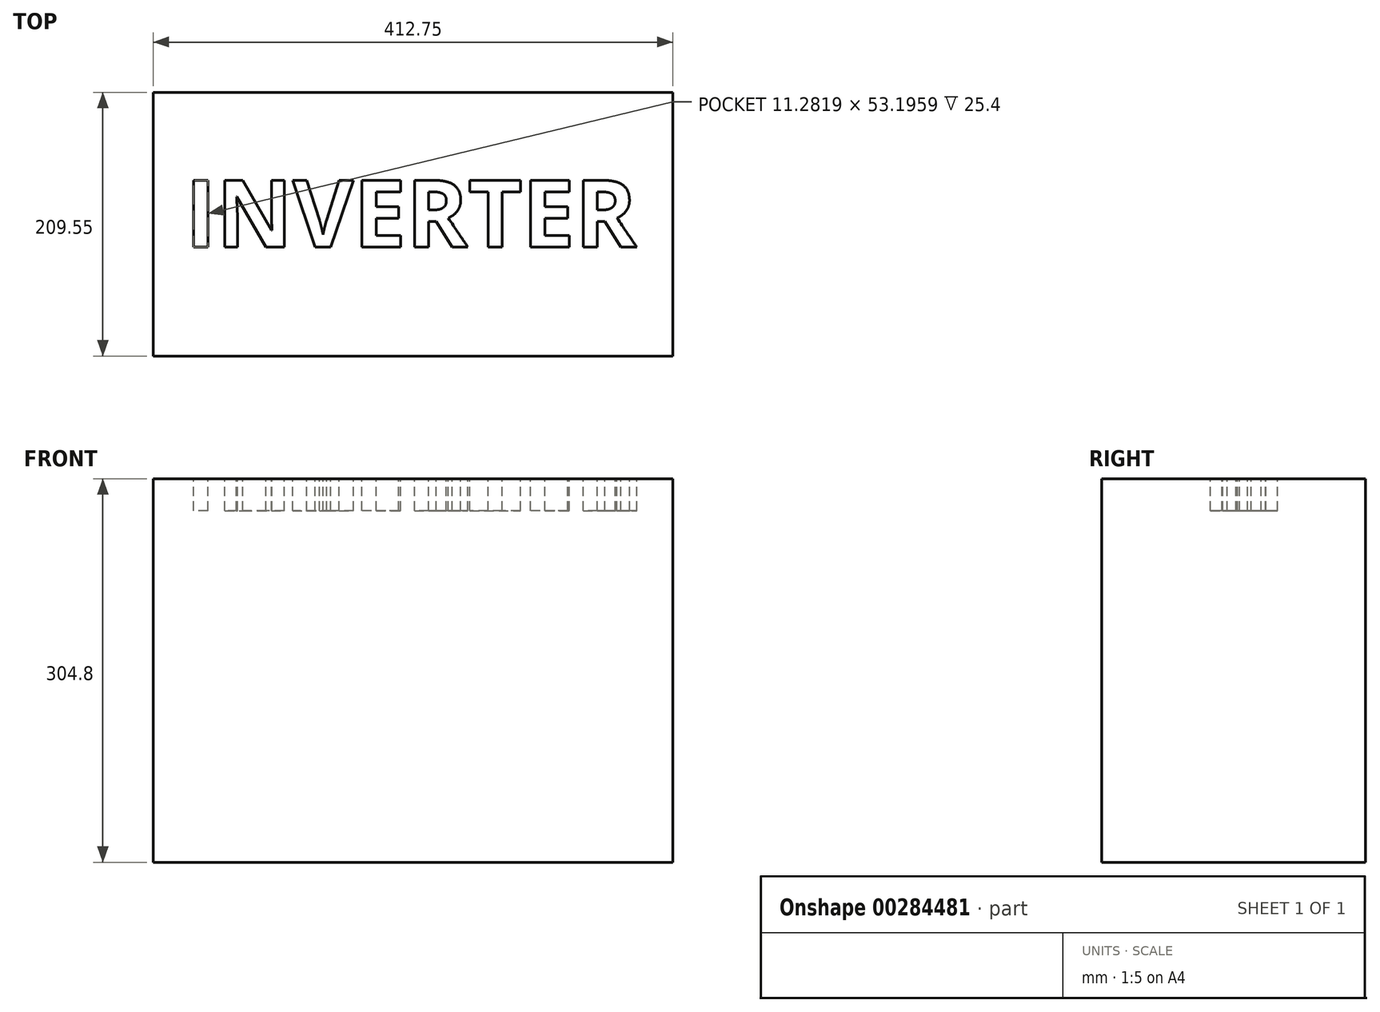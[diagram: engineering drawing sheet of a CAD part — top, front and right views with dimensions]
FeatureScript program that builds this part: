
annotation { "Feature Type Name" : "Feature", "Feature Type Description" : "" }
export const myFeature = defineFeature(function(context is Context, id is Id, definition is map)
    precondition{}
    {
        {
            var Q0;
            Q0=qCreatedBy(makeId("Top.planeOp"),FACE);
            var sketch = newSketch(context, id + "F0", { "sketchPlane" : qUnion([Q0])});
            skLineSegment(sketch, "E0.bottom", {"start": v(0, 0) * mm, "end": v(412.75, 0) * mm});
            skLineSegment(sketch, "E0.top", {"start": v(0, 209.55) * mm, "end": v(412.75, 209.55) * mm});
            skLineSegment(sketch, "E0.left", {"start": v(0, 0) * mm, "end": v(0, 209.55) * mm});
            skLineSegment(sketch, "E0.right", {"start": v(412.75, 0) * mm, "end": v(412.75, 209.55) * mm});
            skSolve(sketch);
        }
        {
            var Q0;
            Q0 = qSketchRegion(id + "F0", true);
            extrude(context, id + "F1", {"entities" : qUnion([Q0]), "depth" : 304.8 * mm});
        }
        {
            var Q0;
            Q0=makeQuery(id+"F1.opExtrude","CAP_FACE",FACE,{"disambiguationData":[OSD([sQuery(id+"F0.wireOp",EDGE,"E0.bottom"),sQuery(id+"F0.wireOp",EDGE,"E0.top"),sQuery(id+"F0.wireOp",EDGE,"E0.left"),sQuery(id+"F0.wireOp",EDGE,"E0.right")])],"isStart":false});
            var sketch = newSketch(context, id + "F2", { "sketchPlane" : qUnion([Q0])});
            skText(sketch, "E1", { "text": "INVERTER", "fontName": "OpenSans-Bold.ttf"});
            const initialGuessF2  = {"E1": [0.0254, 0.08645, 1, 0, 0.05365]};
            skSetInitialGuess(sketch, initialGuessF2);
            skSolve(sketch);
        }
        {
            var Q0;
            Q0 = qSketchRegion(id + "F2", true);
            extrude(context, id + "F3", {"entities" : qUnion([Q0]), "operationType" : NewBodyOperationType.REMOVE, "oppositeDirection" : true, "depth" : 25.4 * mm});
        }
    });
